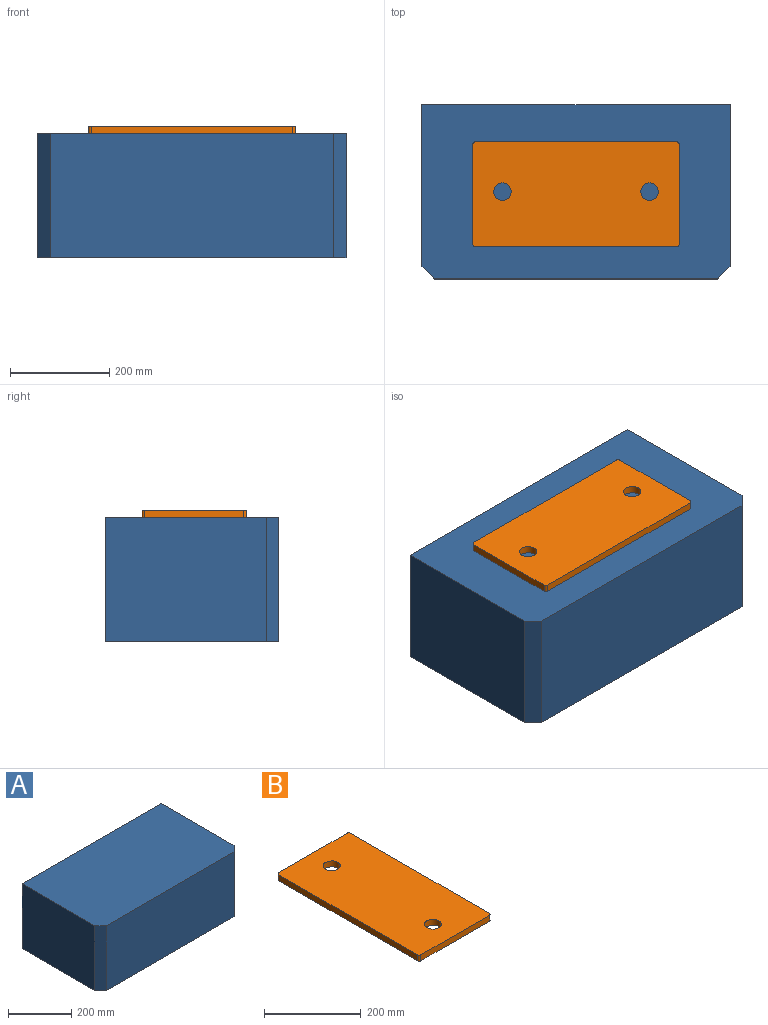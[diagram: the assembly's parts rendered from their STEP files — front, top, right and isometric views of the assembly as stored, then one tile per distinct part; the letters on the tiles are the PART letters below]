
ASSEMBLY  parts=2 mates=1
PART A: 8 faces, bbox 620x350x250 mm
  f0: plane 325x250mm, normal (-1,0,0), area 81250mm2, adj f3,f4,f5,f6
  f1: plane 570x250mm, normal (0,-1,0), area 142500mm2, adj f4,f5,f6,f7
  f2: plane 325x250mm, normal (1,0,0), area 81250mm2, adj f3,f4,f5,f7
  f3: plane 620x250mm, normal (0,1,0), area 155000mm2, adj f0,f2,f4,f5
  f4: plane 620x350mm, normal (0,0,1), area 216375mm2, adj f0,f1,f2,f3,f6,f7
  f5: plane 620x350mm, normal (0,0,-1), area 216375mm2, adj f0,f1,f2,f3,f6,f7
  f6: plane 250x25mm, normal (-0.71,-0.71,0), area 8838.8mm2, adj f0,f1,f4,f5
  f7: plane 250x25mm, normal (0.71,-0.71,0), area 8838.8mm2, adj f1,f2,f4,f5
PART B: 12 faces, bbox 210x416x15 mm
  f0: plane 406x15mm, normal (1,0,0), area 6090mm2, adj f1,f9,f10,f11
  f1: cylinder r=5mm len=15mm, axis (0,0,-1), area 117.8mm2, adj f0,f2,f10,f11
  f2: plane 200x15mm, normal (0,1,0), area 3000mm2, adj f1,f3,f10,f11
  f3: cylinder r=5mm len=15mm, axis (0,0,-1), area 117.8mm2, adj f2,f4,f10,f11
  f4: plane 406x15mm, normal (-1,0,0), area 6090mm2, adj f3,f5,f10,f11
  f5: cylinder r=5mm len=15mm, axis (0,0,-1), area 117.8mm2, adj f4,f6,f10,f11
  f6: plane 200x15mm, normal (0,-1,0), area 3000mm2, adj f5,f9,f10,f11
  f7: cylinder r=17.5mm len=35mm, axis (0,0,-1), area 1649.3mm2, adj f10,f11
  f8: cylinder r=17.5mm len=35mm, axis (0,0,-1), area 1649.3mm2, adj f10,f11
  f9: cylinder r=5mm len=15mm, axis (0,0,-1), area 117.8mm2, adj f0,f6,f10,f11
  f10: plane 416x210mm, normal (0,0,1), area 85414.3mm2, adj f0,f1,f2,f3,f4,f5,f6,f7
  f11: plane 416x210mm, normal (0,0,-1), area 85414.3mm2, adj f0,f1,f2,f3,f4,f5,f6,f7
PLACE A t=(-152.7,-41.79,107.45)mm
PLACE B rot(axis=(0,0,-1),90deg) t=(-148.61,111.51,357.45)mm
MATE parallel A.f4 <-> B.f11  axis (0,0,1) through (-148.61,111.51,357.45)mm
